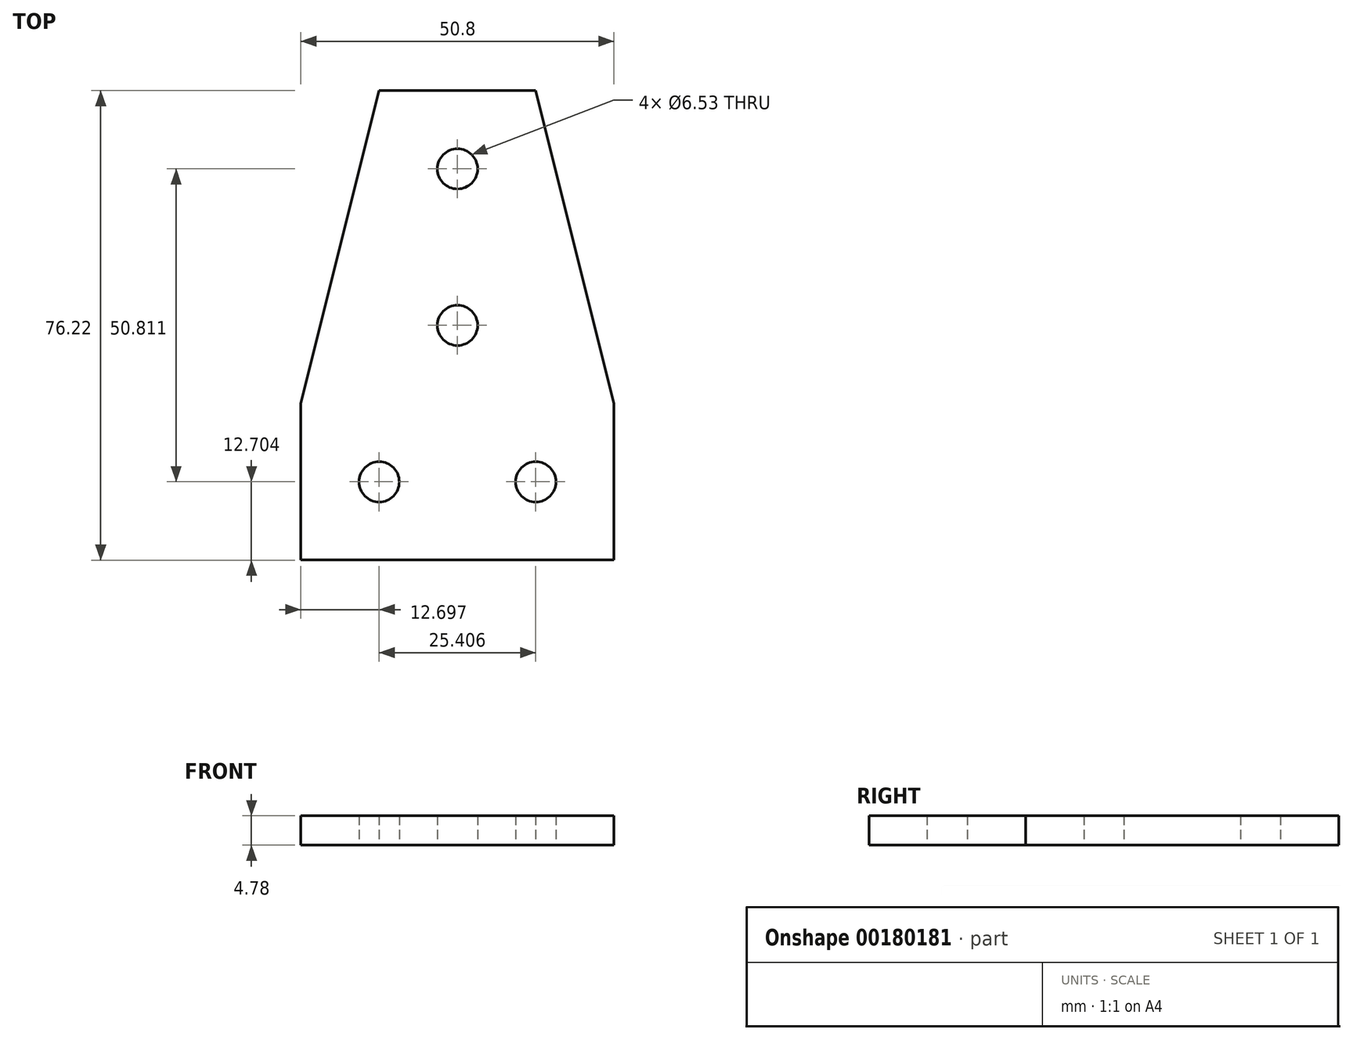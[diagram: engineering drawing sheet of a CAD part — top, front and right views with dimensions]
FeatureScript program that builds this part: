
annotation { "Feature Type Name" : "Feature", "Feature Type Description" : "" }
export const myFeature = defineFeature(function(context is Context, id is Id, definition is map)
    precondition{}
    {
        {
            var Q0;
            Q0=qCreatedBy(makeId("Top.planeOp"),FACE);
            var sketch = newSketch(context, id + "F0", { "sketchPlane" : qUnion([Q0])});
            skLineSegment(sketch, "E0.top", {"start": v(12.7, 38.1) * mm, "end": v(-12.7, 38.1) * mm});
            skPoint(sketch, "E0.middle", {"position": v(0, 0) * mm});
            skLineSegment(sketch, "E1", {"start": v(0, 0) * mm, "end": v(0, -44.44) * mm, "construction": true});
            skLineSegment(sketch, "E2", {"start": v(-25.4, -38.1) * mm, "end": v(-25.4, -12.7) * mm});
            skLineSegment(sketch, "E3", {"start": v(25.4, -12.7) * mm, "end": v(25.4, -38.1) * mm});
            skLineSegment(sketch, "E4", {"start": v(-25.4, -12.7) * mm, "end": v(-12.7, 38.1) * mm});
            skLineSegment(sketch, "E5", {"start": v(12.7, 38.1) * mm, "end": v(25.4, -12.7) * mm});
            skCircle(sketch, "E6", {"center": v(-12.7, -25.4) * mm, "radius": 3.26 * mm});
            skCircle(sketch, "E7.MirrorC", {"center": v(12.7, -25.4) * mm, "radius": 3.26 * mm});
            skLineSegment(sketch, "E8", {"start": v(-25.4, -38.1) * mm, "end": v(25.4, -38.1) * mm});
            skCircle(sketch, "E9", {"center": v(0, 0) * mm, "radius": 3.26 * mm});
            skCircle(sketch, "E10", {"center": v(0, 25.4) * mm, "radius": 3.26 * mm});
            skSolve(sketch);
        }
        {
            var Q0;
            Q0=qSketchRegion(id+"F0",true);
            extrude(context, id + "F1", {"entities" : qUnion([Q0]), "depth" : 4.78 * mm});
        }
    });
